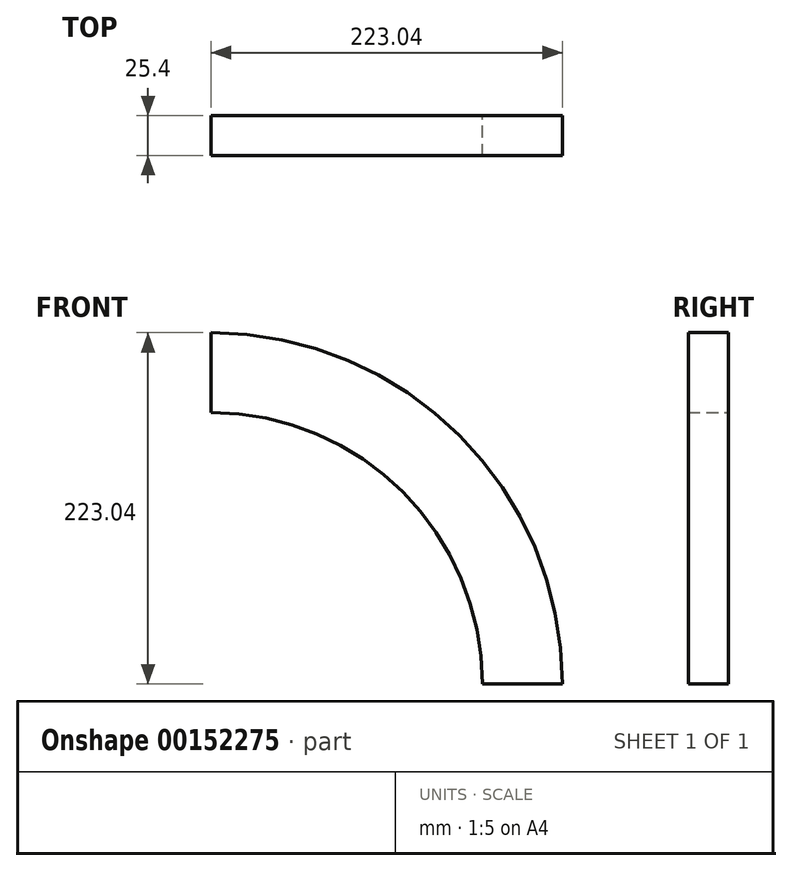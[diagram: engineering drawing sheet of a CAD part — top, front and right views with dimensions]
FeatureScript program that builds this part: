
annotation { "Feature Type Name" : "Feature", "Feature Type Description" : "" }
export const myFeature = defineFeature(function(context is Context, id is Id, definition is map)
    precondition{}
    {
        {
            var Q0;
            Q0=qCreatedBy(makeId("Front.planeOp"),FACE);
            var sketch = newSketch(context, id + "F0", { "sketchPlane" : qUnion([Q0])});
            skArc(sketch, "E0", {"start": v(172.24, 0) * mm, "mid": v(121.8, 121.8) * mm, "end": v(0, 172.24) * mm});
            skArc(sketch, "E1", {"start": v(223.04, 0) * mm, "mid": v(157.72, 157.72) * mm, "end": v(0, 223.04) * mm});
            skLineSegment(sketch, "E2", {"start": v(0, 172.24) * mm, "end": v(0, 223.04) * mm});
            skLineSegment(sketch, "E3", {"start": v(172.24, 0) * mm, "end": v(223.04, 0) * mm});
            skSolve(sketch);
        }
        {
            var Q0;
            Q0=makeQuery(id+"F0.imprint","IMPRINT",FACE,{"disambiguationData":[TD([[makeQuery(id+"F0.imprint","IMPRINT",EDGE,{"derivedFrom":sQuery(id+"F0.wireOp",EDGE,"E0")}),-1.0]])]});
            extrude(context, id + "F1", {"entities" : qUnion([Q0]), "depth" : 25.4 * mm});
        }
    });
